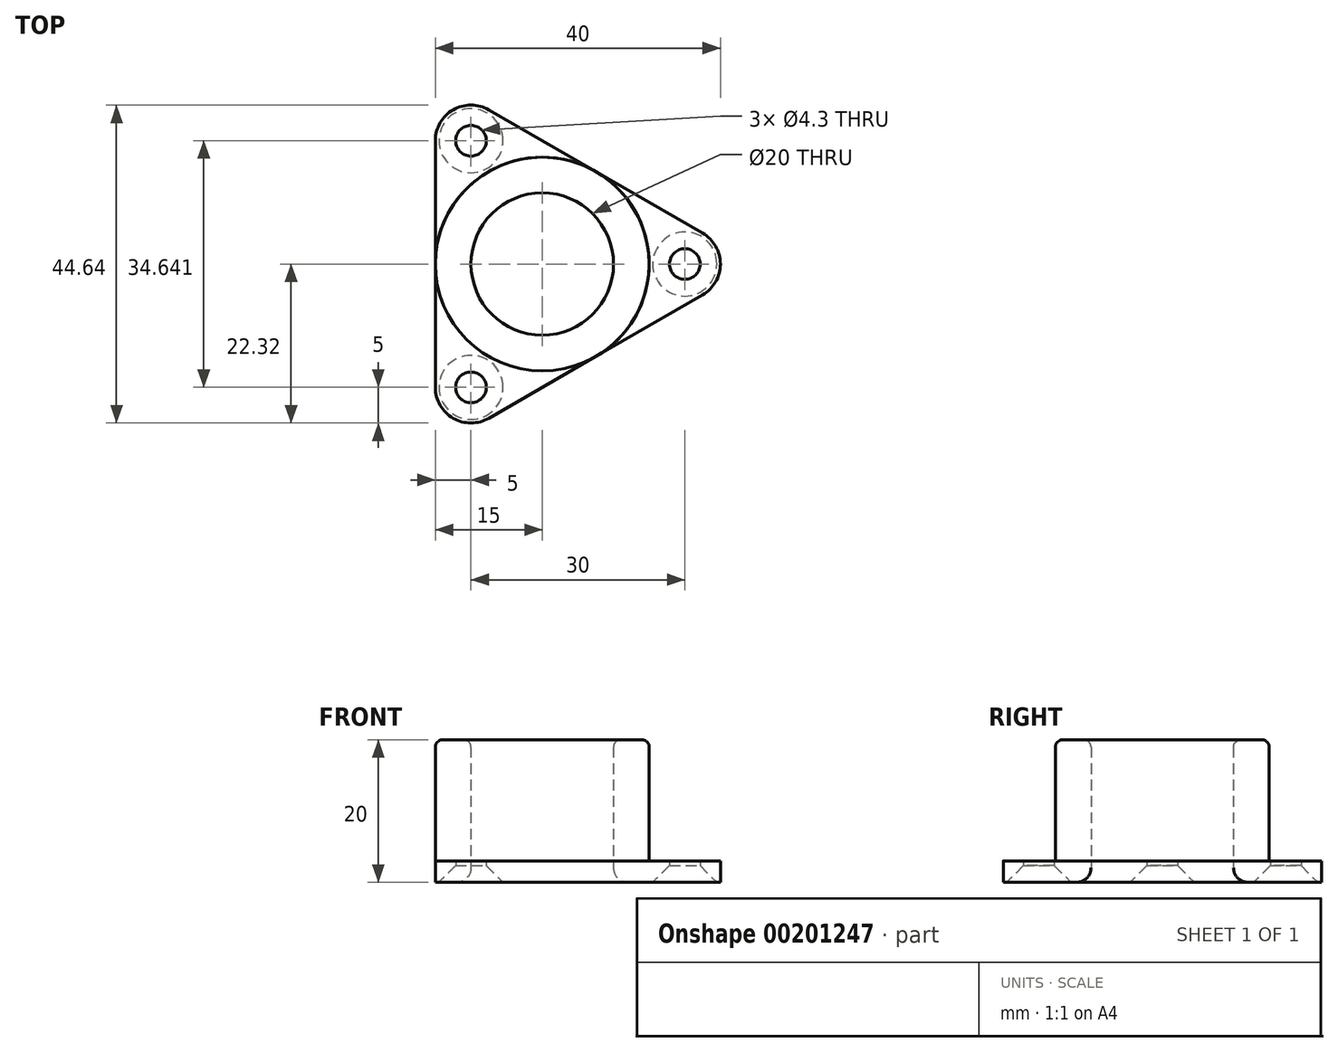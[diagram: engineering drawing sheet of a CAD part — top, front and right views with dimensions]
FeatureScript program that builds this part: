
annotation { "Feature Type Name" : "Feature", "Feature Type Description" : "" }
export const myFeature = defineFeature(function(context is Context, id is Id, definition is map)
    precondition{}
    {
        {
            var Q0;
            Q0=qCreatedBy(makeId("Top.planeOp"),FACE);
            var sketch = newSketch(context, id + "F0", { "sketchPlane" : qUnion([Q0])});
            skLineSegment(sketch, "E0", {"start": v(22.5, 4.33) * mm, "end": v(-7.5, 21.65) * mm});
            skLineSegment(sketch, "E1", {"start": v(-15, 17.32) * mm, "end": v(-15, -17.32) * mm});
            skLineSegment(sketch, "E2", {"start": v(-7.5, -21.65) * mm, "end": v(22.5, -4.33) * mm});
            skPoint(sketch, "E3.visualSharp", {"position": v(-15, 25.98) * mm});
            skArc(sketch, "E3.filletArc", {"start": v(-7.5, 21.65) * mm, "mid": v(-12.5, 21.65) * mm, "end": v(-15, 17.32) * mm});
            skPoint(sketch, "E4.visualSharp", {"position": v(-15, -25.98) * mm});
            skArc(sketch, "E4.filletArc", {"start": v(-15, -17.32) * mm, "mid": v(-12.5, -21.65) * mm, "end": v(-7.5, -21.65) * mm});
            skPoint(sketch, "E5.visualSharp", {"position": v(30, 0) * mm});
            skArc(sketch, "E5.filletArc", {"start": v(22.5, -4.33) * mm, "mid": v(25, 0) * mm, "end": v(22.5, 4.33) * mm});
            skLineSegment(sketch, "E6", {"start": v(0, 0) * mm, "end": v(20, 0) * mm, "construction": true});
            skPoint(sketch, "E6.endSnap0", {"position": v(25, 0) * mm});
            skLineSegment(sketch, "E7", {"start": v(0, 0) * mm, "end": v(-10, 17.32) * mm, "construction": true});
            skLineSegment(sketch, "E8", {"start": v(0, 0) * mm, "end": v(-10, -17.32) * mm, "construction": true});
            skCircle(sketch, "E9", {"center": v(0, 0) * mm, "radius": 15 * mm});
            skCircle(sketch, "E10", {"center": v(0, 0) * mm, "radius": 10 * mm});
            skCircle(sketch, "E11", {"center": v(0, 0) * mm, "radius": 20 * mm, "construction": true});
            skSolve(sketch);
        }
        {
            var Q0;
            Q0=makeQuery(id+"F0.imprint","IMPRINT",FACE,{"disambiguationData":[TD([[makeQuery(id+"F0.imprint","IMPRINT",EDGE,{"derivedFrom":sQuery(id+"F0.wireOp",EDGE,"E10")}),-1.0]])]});
            extrude(context, id + "F1", {"entities" : qUnion([Q0]), "depth" : 20 * mm});
        }
        {
            var Q0;
            {var subQ0=sQuery(id+"F0.wireOp",EDGE,"E3.filletArc");Q0=makeQuery(id+"F0.imprint","IMPRINT",FACE,{"disambiguationData":[TD([[makeQuery(id+"F0.imprint","IMPRINT",EDGE,{"derivedFrom":subQ0}),1.0]])]});}
            var Q1;
            {var subQ0=sQuery(id+"F0.wireOp",EDGE,"E5.filletArc");Q1=makeQuery(id+"F0.imprint","IMPRINT",FACE,{"disambiguationData":[TD([[makeQuery(id+"F0.imprint","IMPRINT",EDGE,{"derivedFrom":subQ0}),1.0]])]});}
            var Q2;
            {var subQ0=sQuery(id+"F0.wireOp",EDGE,"E4.filletArc");Q2=makeQuery(id+"F0.imprint","IMPRINT",FACE,{"disambiguationData":[TD([[makeQuery(id+"F0.imprint","IMPRINT",EDGE,{"derivedFrom":subQ0}),1.0]])]});}
            extrude(context, id + "F2", {"entities" : qUnion([Q0, Q1, Q2]), "operationType" : NewBodyOperationType.ADD, "depth" : 3 * mm});
        }
        {
            var Q0;
            Q0=sQuery(id+"F0.wireOp",VERTEX,"E5.filletArc.center");
            var Q1;
            Q1=sQuery(id+"F0.wireOp",VERTEX,"E8.end");
            var Q2;
            Q2=sQuery(id+"F0.wireOp",VERTEX,"E7.end");
            var Q3;
            Q3=makeQuery(id+"F1.opExtrude","SWEPT_BODY",BODY,{"disambiguationData":[OSD([sQuery(id+"F0.wireOp",EDGE,"E9"),sQuery(id+"F0.wireOp",EDGE,"E10")])]});
            hole(context, id + "F3", {"style" : HoleStyle.C_SINK, "endStyle" : HoleEndStyle.THROUGH, "oppositeDirection" : true, "holeDiameter" : 4.3 * mm, "cSinkDiameter" : 9 * mm, "cSinkAngle" : 90 * degree, "isTappedThrough" : true, "tappedDepth" : 7.6 * mm, "tapClearance" : 3, "startFromSketch" : true, "locations" : qUnion([Q0, Q1, Q2]), "scope" : qUnion([Q3])});
        }
        {
            var Q0;
            Q0=makeQuery(id+"F1.opExtrude","CAP_EDGE",EDGE,{"disambiguationData":[OSD([sQuery(id+"F0.wireOp",EDGE,"E10")])],"isStart":true});
            fillet(context, id + "F4", {"entities" : qUnion([Q0]), "radius" : 2 * mm, "tangentPropagation" : true, "allowEdgeOverflow" : false});
        }
        {
            var Q0;
            Q0=makeQuery(id+"F1.opExtrude","CAP_EDGE",EDGE,{"disambiguationData":[OSD([sQuery(id+"F0.wireOp",EDGE,"E9")])],"isStart":false});
            var Q1;
            Q1=makeQuery(id+"F1.opExtrude","CAP_EDGE",EDGE,{"disambiguationData":[OSD([sQuery(id+"F0.wireOp",EDGE,"E10")])],"isStart":false});
            fillet(context, id + "F5", {"entities" : qUnion([Q0, Q1]), "radius" : 1 * mm, "tangentPropagation" : true, "allowEdgeOverflow" : false});
        }
    });
